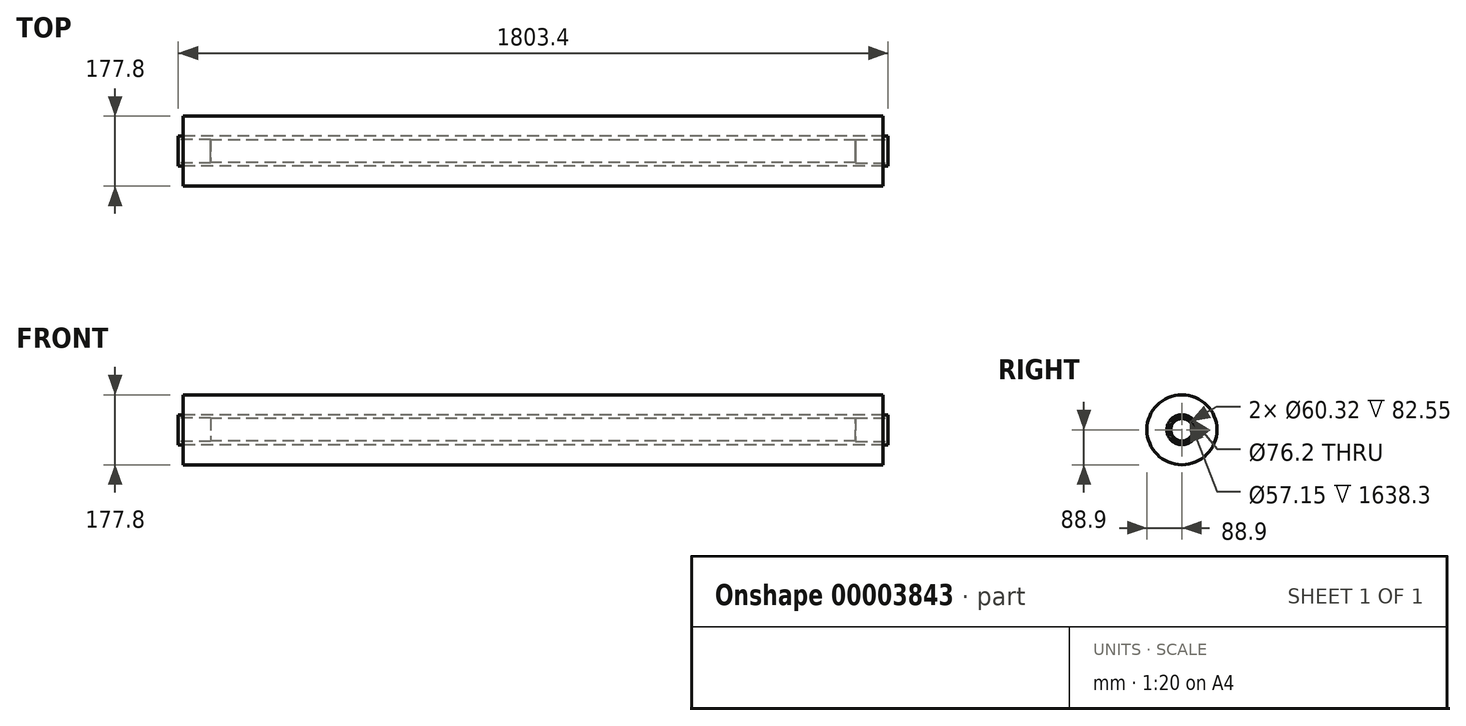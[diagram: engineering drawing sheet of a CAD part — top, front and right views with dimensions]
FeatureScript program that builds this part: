
annotation { "Feature Type Name" : "Feature", "Feature Type Description" : "" }
export const myFeature = defineFeature(function(context is Context, id is Id, definition is map)
    precondition{}
    {
        {
            var Q0;
            Q0=qCreatedBy(makeId("Right.planeOp"),FACE);
            var sketch = newSketch(context, id + "F0", { "sketchPlane" : qUnion([Q0])});
            skCircle(sketch, "E0", {"center": v(0, 0) * mm, "radius": 38.1 * mm});
            skCircle(sketch, "E1", {"center": v(0, 0) * mm, "radius": 28.58 * mm});
            skSolve(sketch);
        }
        {
            var Q0;
            Q0=makeQuery(id+"F0.imprint","IMPRINT",FACE,{"disambiguationData":[TD([[makeQuery(id+"F0.imprint","IMPRINT",EDGE,{"derivedFrom":sQuery(id+"F0.wireOp",EDGE,"E0")}),1.0]])]});
            extrude(context, id + "F1", {"entities" : qUnion([Q0]), "endBound" : BoundingType.SYMMETRIC, "depth" : 1803.4 * mm});
        }
        {
            var Q0;
            Q0=makeQuery(id+"F1.opExtrude","CAP_FACE",FACE,{"disambiguationData":[OSD([sQuery(id+"F0.wireOp",EDGE,"E0"),sQuery(id+"F0.wireOp",EDGE,"E1")])],"isStart":false});
            var sketch = newSketch(context, id + "F2", { "sketchPlane" : qUnion([Q0])});
            skCircle(sketch, "E2", {"center": v(0, 0) * mm, "radius": 30.16 * mm});
            skSolve(sketch);
        }
        {
            var Q0;
            {var subQ0=makeQuery(id+"F2.imprint","IMPRINT",EDGE,{"derivedFrom":makeQuery(id+"F1.opExtrude","CAP_EDGE",EDGE,{"disambiguationData":[OSD([sQuery(id+"F0.wireOp",EDGE,"E1")])],"isStart":false})});Q0=qUnion([makeQuery(id+"F2.imprint","IMPRINT",FACE,{"disambiguationData":[TD([[subQ0,1.0]])]}),makeQuery(id+"F2.imprint","IMPRINT",FACE,{"disambiguationData":[TD([[makeQuery(id+"F2.imprint","IMPRINT",EDGE,{"derivedFrom":sQuery(id+"F2.wireOp",EDGE,"E2")}),1.0]])]})]);}
            extrude(context, id + "F3", {"entities" : qUnion([Q0]), "operationType" : NewBodyOperationType.REMOVE, "oppositeDirection" : true, "depth" : 82.55 * mm});
        }
        {
            var Q0;
            Q0=makeQuery(id+"F1.opExtrude","CAP_FACE",FACE,{"disambiguationData":[OSD([sQuery(id+"F0.wireOp",EDGE,"E0"),sQuery(id+"F0.wireOp",EDGE,"E1")])],"isStart":true});
            var sketch = newSketch(context, id + "F4", { "sketchPlane" : qUnion([Q0])});
            skCircle(sketch, "E3", {"center": v(0, 0) * mm, "radius": 30.16 * mm});
            skSolve(sketch);
        }
        {
            var Q0;
            {var subQ0=makeQuery(id+"F4.imprint","IMPRINT",EDGE,{"derivedFrom":makeQuery(id+"F1.opExtrude","CAP_EDGE",EDGE,{"disambiguationData":[OSD([sQuery(id+"F0.wireOp",EDGE,"E1")])],"isStart":true})});Q0=qUnion([makeQuery(id+"F4.imprint","IMPRINT",FACE,{"disambiguationData":[TD([[subQ0,-1.0]])]}),makeQuery(id+"F4.imprint","IMPRINT",FACE,{"disambiguationData":[TD([[makeQuery(id+"F4.imprint","IMPRINT",EDGE,{"derivedFrom":sQuery(id+"F4.wireOp",EDGE,"E3")}),1.0]])]})]);}
            extrude(context, id + "F5", {"entities" : qUnion([Q0]), "operationType" : NewBodyOperationType.REMOVE, "oppositeDirection" : true, "depth" : 82.55 * mm});
        }
        {
            var Q0;
            Q0=qCreatedBy(makeId("Right.planeOp"),FACE);
            var sketch = newSketch(context, id + "F6", { "sketchPlane" : qUnion([Q0])});
            skCircle(sketch, "E4", {"center": v(0, 0) * mm, "radius": 88.9 * mm});
            skCircle(sketch, "E5", {"center": v(0, 0) * mm, "radius": 38.1 * mm});
            skSolve(sketch);
        }
        {
            var Q0;
            Q0=makeQuery(id+"F6.imprint","IMPRINT",FACE,{"disambiguationData":[TD([[makeQuery(id+"F6.imprint","IMPRINT",EDGE,{"derivedFrom":sQuery(id+"F6.wireOp",EDGE,"E4")}),1.0]])]});
            extrude(context, id + "F7", {"entities" : qUnion([Q0]), "endBound" : BoundingType.SYMMETRIC, "depth" : 1778 * mm});
        }
    });
